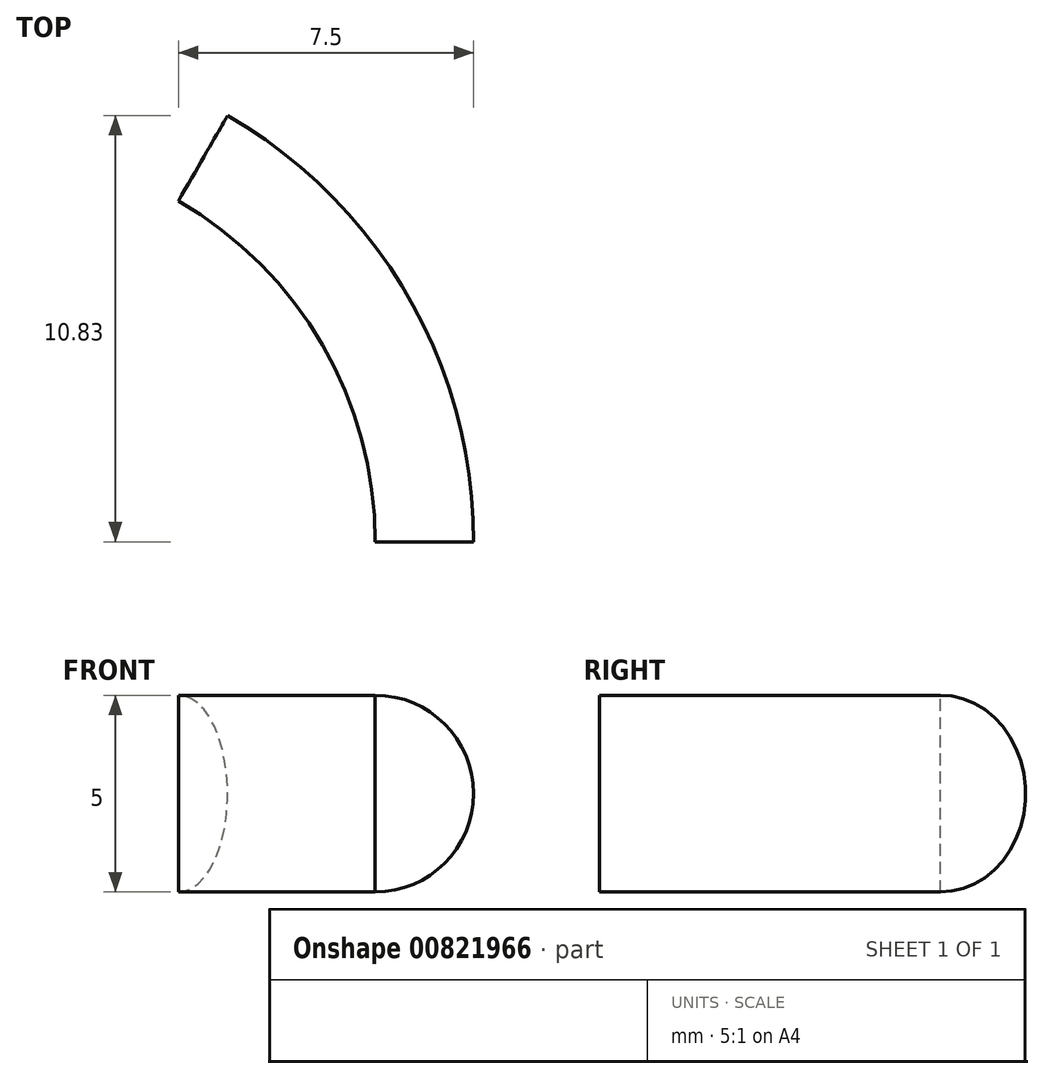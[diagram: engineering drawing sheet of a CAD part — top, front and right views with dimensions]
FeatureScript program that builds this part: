
annotation { "Feature Type Name" : "Feature", "Feature Type Description" : "" }
export const myFeature = defineFeature(function(context is Context, id is Id, definition is map)
    precondition{}
    {
        {
            var Q0;
            Q0=qCreatedBy(makeId("Front.planeOp"),FACE);
            var sketch = newSketch(context, id + "F0", { "sketchPlane" : qUnion([Q0])});
            skLineSegment(sketch, "E0", {"start": v(0, 0) * mm, "end": v(0, 5) * mm});
            skArc(sketch, "E1", {"start": v(0, 0) * mm, "mid": v(2.5, 2.5) * mm, "end": v(0, 5) * mm});
            skLineSegment(sketch, "E2", {"start": v(0, 0) * mm, "end": v(-10, 0) * mm});
            skLineSegment(sketch, "E3", {"start": v(-10, 0) * mm, "end": v(-10, 18.8) * mm});
            skSolve(sketch);
        }
        {
            var Q0;
            Q0=qSketchRegion(id+"F0",true);
            var Q1;
            Q1=sQuery(id+"F0.wireOp",EDGE,"E3");
            revolve(context, id + "F1", {"surfaceOperationType" : NewSurfaceOperationType.NEW, "entities" : qUnion([Q0]), "axis" : qUnion([Q1]), "revolveType" : RevolveType.ONE_DIRECTION, "angle" : 60 * degree});
        }
    });
